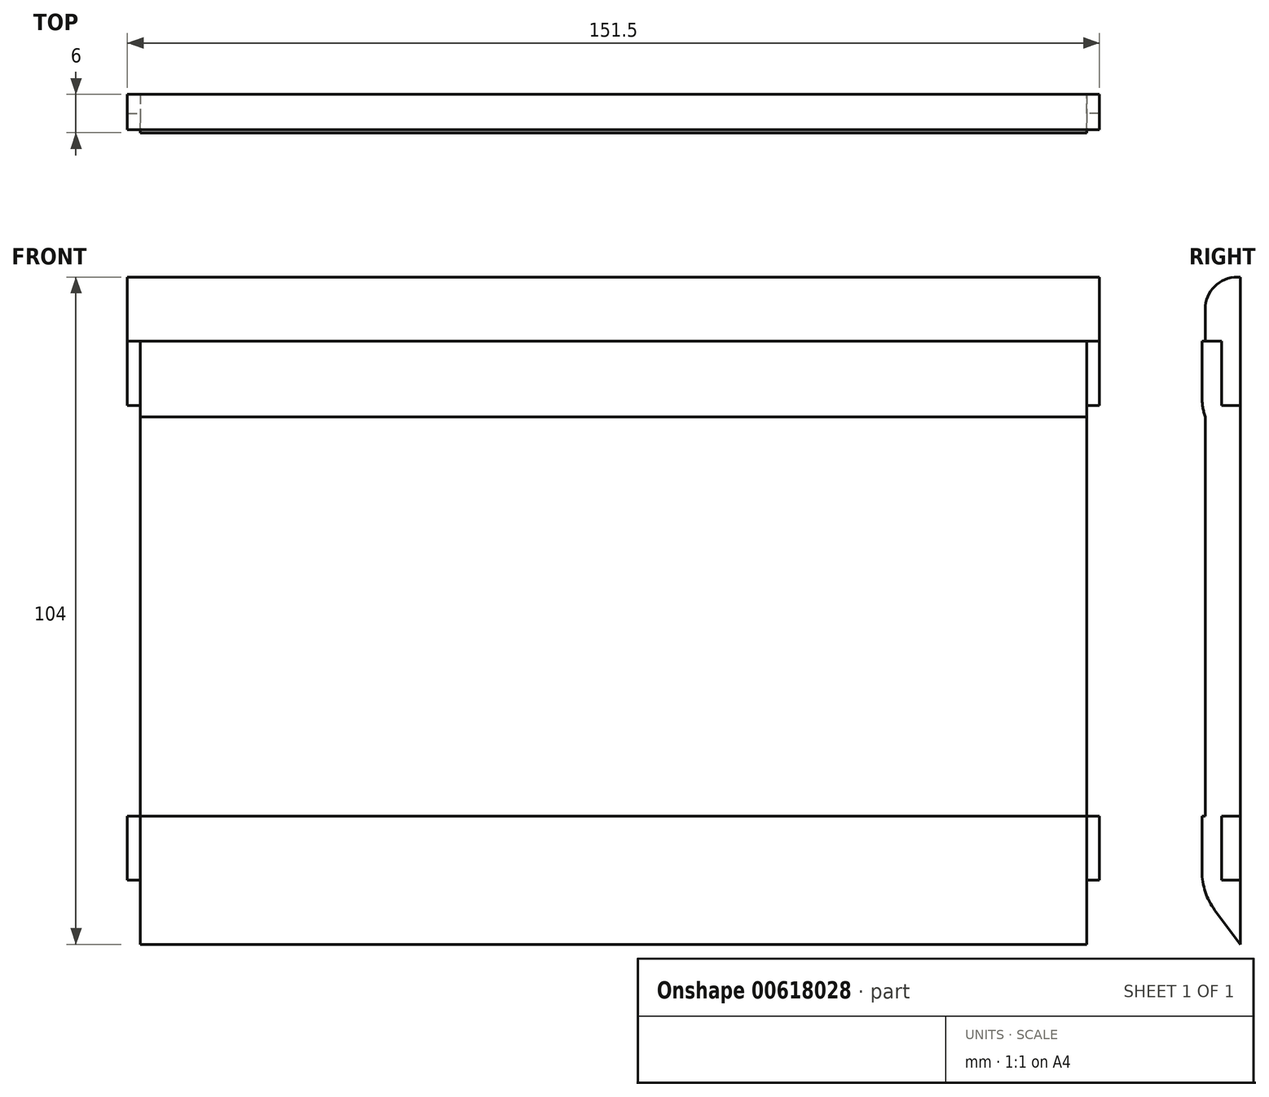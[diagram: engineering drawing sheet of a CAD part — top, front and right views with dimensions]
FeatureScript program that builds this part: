
annotation { "Feature Type Name" : "Feature", "Feature Type Description" : "" }
export const myFeature = defineFeature(function(context is Context, id is Id, definition is map)
    precondition{}
    {
        {
            var Q0;
            Q0=qCreatedBy(makeId("Right.planeOp"),FACE);
            var sketch = newSketch(context, id + "F0", { "sketchPlane" : qUnion([Q0])});
            skLineSegment(sketch, "E0", {"start": v(35.95, 58.2) * mm, "end": v(35.95, -45.8) * mm});
            skLineSegment(sketch, "E1", {"start": v(35.95, 38.2) * mm, "end": v(32.95, 38.2) * mm});
            skLineSegment(sketch, "E2", {"start": v(32.95, 38.2) * mm, "end": v(32.95, 48.2) * mm});
            skLineSegment(sketch, "E3", {"start": v(32.95, 48.2) * mm, "end": v(29.95, 48.2) * mm});
            skLineSegment(sketch, "E4", {"start": v(29.95, 48.2) * mm, "end": v(29.95, 36.2) * mm});
            skLineSegment(sketch, "E5", {"start": v(29.95, 36.2) * mm, "end": v(35.95, 28.2) * mm});
            skLineSegment(sketch, "E6", {"start": v(35.95, -45.8) * mm, "end": v(29.95, -37.8) * mm});
            skLineSegment(sketch, "E7", {"start": v(29.95, -37.8) * mm, "end": v(29.95, -25.8) * mm});
            skLineSegment(sketch, "E8", {"start": v(29.95, -25.8) * mm, "end": v(32.95, -25.8) * mm});
            skLineSegment(sketch, "E9", {"start": v(32.95, -25.8) * mm, "end": v(32.95, -35.8) * mm});
            skLineSegment(sketch, "E10", {"start": v(32.95, -35.8) * mm, "end": v(35.95, -35.8) * mm});
            skSolve(sketch);
        }
        {
            var Q0;
            {var subQ0=sQuery(id+"F0.wireOp",EDGE,"E1");Q0=makeQuery(id+"F0.imprint","IMPRINT",FACE,{"disambiguationData":[TD([[makeQuery(id+"F0.imprint","IMPRINT",EDGE,{"derivedFrom":subQ0}),1.0]])]});}
            var Q1;
            {var subQ0=sQuery(id+"F0.wireOp",EDGE,"E6");Q1=makeQuery(id+"F0.imprint","IMPRINT",FACE,{"disambiguationData":[TD([[makeQuery(id+"F0.imprint","IMPRINT",EDGE,{"derivedFrom":subQ0}),-1.0]])]});}
            extrude(context, id + "F1", {"entities" : qUnion([Q0, Q1]), "depth" : 147.5 * mm, "offsetDistance" : 25 * mm});
        }
        {
            var Q0;
            Q0=makeQuery(id+"F1.opExtrude","SWEPT_EDGE",EDGE,{"disambiguationData":[OSD([sQuery(id+"F0.wireOp",EDGE,"E4"),sQuery(id+"F0.wireOp",EDGE,"E5")])]});
            var Q1;
            Q1=makeQuery(id+"F1.opExtrude","SWEPT_EDGE",EDGE,{"disambiguationData":[OSD([sQuery(id+"F0.wireOp",EDGE,"E6"),sQuery(id+"F0.wireOp",EDGE,"E7")])]});
            fillet(context, id + "F2", {"entities" : qUnion([Q0, Q1]), "radius" : 10 * mm, "tangentPropagation" : true, "allowEdgeOverflow" : false});
        }
        {
            var Q0;
            Q0=makeQuery(id+"F1.opExtrude","CAP_FACE",FACE,{"disambiguationData":[OSD([sQuery(id+"F0.wireOp",EDGE,"E0"),sQuery(id+"F0.wireOp",EDGE,"E6"),sQuery(id+"F0.wireOp",EDGE,"E7"),sQuery(id+"F0.wireOp",EDGE,"E8"),sQuery(id+"F0.wireOp",EDGE,"E9"),sQuery(id+"F0.wireOp",EDGE,"E10")])],"isStart":true});
            var sketch = newSketch(context, id + "F3", { "sketchPlane" : qUnion([Q0])});
            skLineSegment(sketch, "E11.bottom", {"start": v(-35.95, 58.2) * mm, "end": v(-30.45, 58.2) * mm});
            skLineSegment(sketch, "E11.top", {"start": v(-35.95, -45.8) * mm, "end": v(-30.45, -45.8) * mm});
            skLineSegment(sketch, "E11.left", {"start": v(-35.95, 58.2) * mm, "end": v(-35.95, -45.8) * mm});
            skLineSegment(sketch, "E11.right", {"start": v(-30.45, 58.2) * mm, "end": v(-30.45, -45.8) * mm});
            skSolve(sketch);
        }
        {
            var Q0;
            {var subQ1=sQuery(id+"F3.wireOp",EDGE,"E11.bottom");Q0=makeQuery(id+"F3.imprint","IMPRINT",FACE,{"disambiguationData":[TD([[makeQuery(id+"F3.imprint","IMPRINT",EDGE,{"derivedFrom":subQ1}),-1.0]])]});}
            extrude(context, id + "F4", {"entities" : qUnion([Q0]), "oppositeDirection" : true, "depth" : 147.5 * mm, "offsetDistance" : 25 * mm});
        }
        {
            var Q0;
            Q0=makeQuery(id+"F4.opExtrude","CAP_FACE",FACE,{"disambiguationData":[OSD([sQuery(id+"F0.wireOp",EDGE,"E8"),sQuery(id+"F0.wireOp",EDGE,"E9"),sQuery(id+"F0.wireOp",EDGE,"E10"),sQuery(id+"F3.wireOp",EDGE,"E11.bottom"),sQuery(id+"F3.wireOp",EDGE,"E11.left"),sQuery(id+"F3.wireOp",EDGE,"E11.right")])],"isStart":true});
            var sketch = newSketch(context, id + "F5", { "sketchPlane" : qUnion([Q0])});
            skLineSegment(sketch, "E12.bottom", {"start": v(-35.95, 38.2) * mm, "end": v(-33, 38.2) * mm});
            skLineSegment(sketch, "E12.top", {"start": v(-35.95, 48.2) * mm, "end": v(-33, 48.2) * mm});
            skLineSegment(sketch, "E12.left", {"start": v(-35.95, 38.2) * mm, "end": v(-35.95, 48.2) * mm});
            skLineSegment(sketch, "E12.right", {"start": v(-33, 38.2) * mm, "end": v(-33, 48.2) * mm});
            skLineSegment(sketch, "E13.bottom", {"start": v(-35.95, -25.8) * mm, "end": v(-33, -25.8) * mm});
            skLineSegment(sketch, "E13.top", {"start": v(-35.95, -35.8) * mm, "end": v(-33, -35.8) * mm});
            skLineSegment(sketch, "E13.left", {"start": v(-35.95, -25.8) * mm, "end": v(-35.95, -35.8) * mm});
            skLineSegment(sketch, "E13.right", {"start": v(-33, -25.8) * mm, "end": v(-33, -35.8) * mm});
            skSolve(sketch);
        }
        {
            var Q0;
            Q0 = qSketchRegion(id + "F5", true);
            extrude(context, id + "F6", {"entities" : qUnion([Q0]), "operationType" : NewBodyOperationType.ADD, "depth" : 2 * mm, "offsetDistance" : 25 * mm});
        }
        {
            var Q0;
            Q0=makeQuery(id+"F4.opExtrude","CAP_FACE",FACE,{"disambiguationData":[OSD([sQuery(id+"F0.wireOp",EDGE,"E8"),sQuery(id+"F0.wireOp",EDGE,"E9"),sQuery(id+"F0.wireOp",EDGE,"E10"),sQuery(id+"F3.wireOp",EDGE,"E11.bottom"),sQuery(id+"F3.wireOp",EDGE,"E11.left"),sQuery(id+"F3.wireOp",EDGE,"E11.right")])],"isStart":false});
            var sketch = newSketch(context, id + "F7", { "sketchPlane" : qUnion([Q0])});
            skLineSegment(sketch, "E14.bottom", {"start": v(35.95, 38.2) * mm, "end": v(33, 38.2) * mm});
            skLineSegment(sketch, "E14.top", {"start": v(35.95, 48.2) * mm, "end": v(33, 48.2) * mm});
            skLineSegment(sketch, "E14.left", {"start": v(35.95, 38.2) * mm, "end": v(35.95, 48.2) * mm});
            skLineSegment(sketch, "E14.right", {"start": v(33, 38.2) * mm, "end": v(33, 48.2) * mm});
            skLineSegment(sketch, "E15.bottom", {"start": v(33, -25.8) * mm, "end": v(35.95, -25.8) * mm});
            skLineSegment(sketch, "E15.top", {"start": v(33, -35.8) * mm, "end": v(35.95, -35.8) * mm});
            skLineSegment(sketch, "E15.left", {"start": v(33, -25.8) * mm, "end": v(33, -35.8) * mm});
            skLineSegment(sketch, "E15.right", {"start": v(35.95, -25.8) * mm, "end": v(35.95, -35.8) * mm});
            skSolve(sketch);
        }
        {
            var Q0;
            Q0 = qSketchRegion(id + "F7", true);
            extrude(context, id + "F8", {"entities" : qUnion([Q0]), "operationType" : NewBodyOperationType.ADD, "depth" : 2 * mm, "offsetDistance" : 25 * mm});
        }
        {
            var Q0;
            Q0=makeQuery(id+"F4.opExtrude","SWEPT_EDGE",EDGE,{"disambiguationData":[OSD([sQuery(id+"F3.wireOp",EDGE,"E11.bottom"),sQuery(id+"F3.wireOp",EDGE,"E11.right")])]});
            fillet(context, id + "F9", {"entities" : qUnion([Q0]), "radius" : 5 * mm, "tangentPropagation" : true, "allowEdgeOverflow" : false});
        }
        {
            var Q0;
            Q0=makeQuery(id+"F4.opExtrude","CAP_FACE",FACE,{"disambiguationData":[OSD([sQuery(id+"F0.wireOp",EDGE,"E8"),sQuery(id+"F0.wireOp",EDGE,"E9"),sQuery(id+"F0.wireOp",EDGE,"E10"),sQuery(id+"F3.wireOp",EDGE,"E11.bottom"),sQuery(id+"F3.wireOp",EDGE,"E11.left"),sQuery(id+"F3.wireOp",EDGE,"E11.right")])],"isStart":true});
            var sketch = newSketch(context, id + "F10", { "sketchPlane" : qUnion([Q0])});
            skLineSegment(sketch, "E16", {"start": v(-33, 48.2) * mm, "end": v(-30.45, 48.2) * mm});
            skSolve(sketch);
        }
        {
            var Q0;
            {var subQ5=sQuery(id+"F10.wireOp",EDGE,"E16");Q0=makeQuery(id+"F10.imprint","IMPRINT",FACE,{"disambiguationData":[TD([[makeQuery(id+"F10.imprint","IMPRINT",EDGE,{"derivedFrom":subQ5}),1.0]])]});}
            extrude(context, id + "F11", {"entities" : qUnion([Q0]), "operationType" : NewBodyOperationType.ADD, "depth" : 2 * mm, "offsetDistance" : 25 * mm});
        }
        {
            var Q0;
            Q0=makeQuery(id+"F4.opExtrude","CAP_FACE",FACE,{"disambiguationData":[OSD([sQuery(id+"F0.wireOp",EDGE,"E8"),sQuery(id+"F0.wireOp",EDGE,"E9"),sQuery(id+"F0.wireOp",EDGE,"E10"),sQuery(id+"F3.wireOp",EDGE,"E11.bottom"),sQuery(id+"F3.wireOp",EDGE,"E11.left"),sQuery(id+"F3.wireOp",EDGE,"E11.right")])],"isStart":false});
            var sketch = newSketch(context, id + "F12", { "sketchPlane" : qUnion([Q0])});
            skLineSegment(sketch, "E17", {"start": v(33, 48.2) * mm, "end": v(30.45, 48.2) * mm});
            skSolve(sketch);
        }
        {
            var Q0;
            {var subQ5=sQuery(id+"F12.wireOp",EDGE,"E17");Q0=makeQuery(id+"F12.imprint","IMPRINT",FACE,{"disambiguationData":[TD([[makeQuery(id+"F12.imprint","IMPRINT",EDGE,{"derivedFrom":subQ5}),-1.0]])]});}
            extrude(context, id + "F13", {"entities" : qUnion([Q0]), "operationType" : NewBodyOperationType.ADD, "depth" : 2 * mm, "offsetDistance" : 25 * mm});
        }
    });
